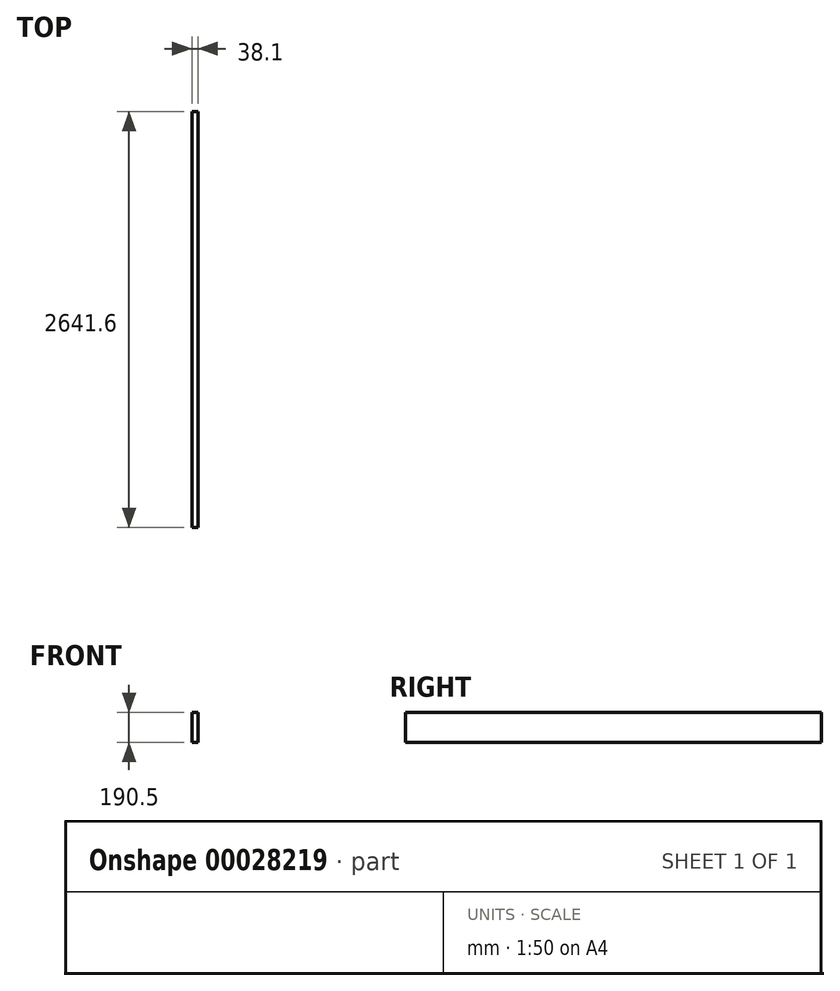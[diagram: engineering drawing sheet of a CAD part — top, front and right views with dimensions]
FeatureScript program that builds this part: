
annotation { "Feature Type Name" : "Feature", "Feature Type Description" : "" }
export const myFeature = defineFeature(function(context is Context, id is Id, definition is map)
    precondition{}
    {
        {
            var Q0;
            Q0=qCreatedBy(makeId("Front.planeOp"),FACE);
            var sketch = newSketch(context, id + "F0", { "sketchPlane" : qUnion([Q0])});
            skLineSegment(sketch, "E0.bottom", {"start": v(-32.53, 183.82) * mm, "end": v(5.57, 183.82) * mm});
            skLineSegment(sketch, "E0.top", {"start": v(-32.53, -6.68) * mm, "end": v(5.57, -6.68) * mm});
            skLineSegment(sketch, "E0.left", {"start": v(-32.53, 183.82) * mm, "end": v(-32.53, -6.68) * mm});
            skLineSegment(sketch, "E0.right", {"start": v(5.57, 183.82) * mm, "end": v(5.57, -6.68) * mm});
            skSolve(sketch);
        }
        {
            var Q0;
            Q0=makeQuery(id+"F0.imprint","IMPRINT",FACE,{"disambiguationData":[TD([[makeQuery(id+"F0.imprint","IMPRINT",EDGE,{"derivedFrom":sQuery(id+"F0.wireOp",EDGE,"E0.bottom")}),-1.0]])]});
            extrude(context, id + "F1", {"entities" : qUnion([Q0]), "depth" : 2641.6 * mm});
        }
    });
